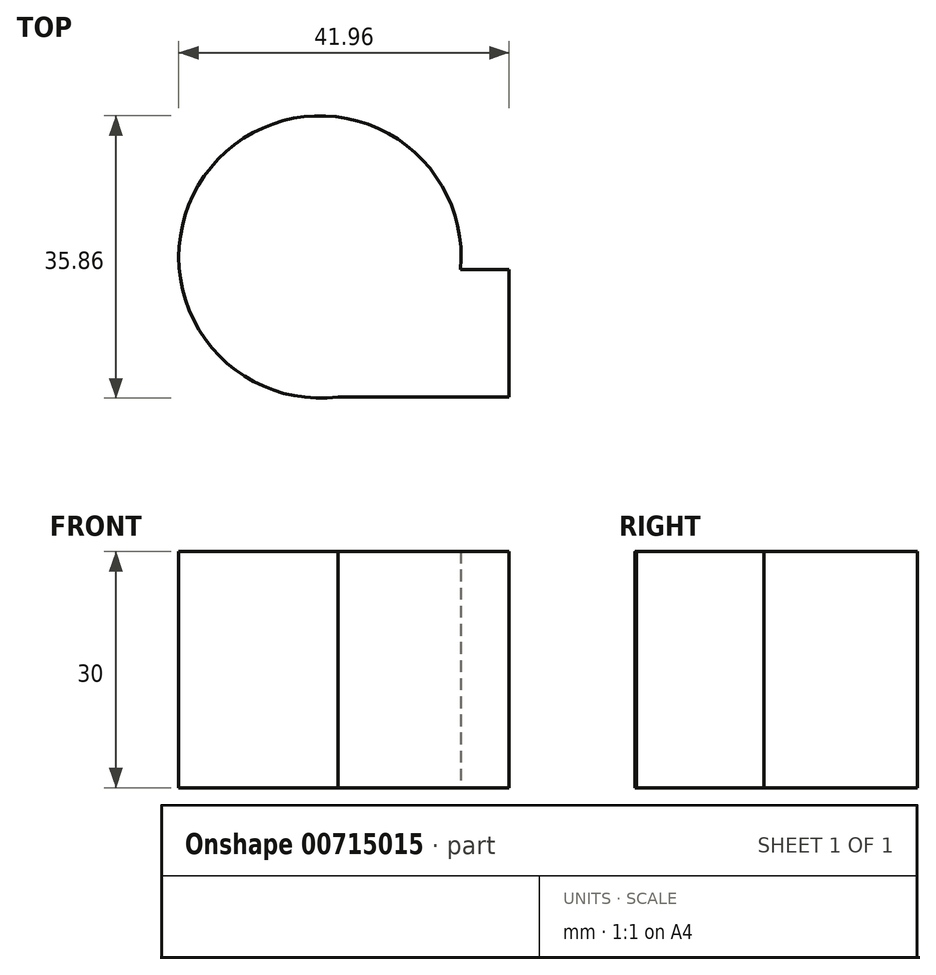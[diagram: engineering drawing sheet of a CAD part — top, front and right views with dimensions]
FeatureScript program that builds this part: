
annotation { "Feature Type Name" : "Feature", "Feature Type Description" : "" }
export const myFeature = defineFeature(function(context is Context, id is Id, definition is map)
    precondition{}
    {
        {
            var Q0;
            Q0=qCreatedBy(makeId("Top.planeOp"),FACE);
            var sketch = newSketch(context, id + "F0", { "sketchPlane" : qUnion([Q0])});
            skLineSegment(sketch, "E0.bottom", {"start": v(-31.12, 24.11) * mm, "end": v(50.55, 24.11) * mm});
            skLineSegment(sketch, "E0.top", {"start": v(-31.12, -36.94) * mm, "end": v(50.55, -36.94) * mm});
            skLineSegment(sketch, "E0.left", {"start": v(-31.12, 24.11) * mm, "end": v(-31.12, -36.94) * mm});
            skLineSegment(sketch, "E0.right", {"start": v(50.55, 24.11) * mm, "end": v(50.55, -36.94) * mm});
            skLineSegment(sketch, "E1.bottom", {"start": v(0, -1.6) * mm, "end": v(24.03, -1.6) * mm});
            skLineSegment(sketch, "E1.top", {"start": v(0, -17.78) * mm, "end": v(24.03, -17.78) * mm});
            skLineSegment(sketch, "E1.left", {"start": v(0, -1.6) * mm, "end": v(0, -17.78) * mm});
            skLineSegment(sketch, "E1.right", {"start": v(24.03, -1.6) * mm, "end": v(24.03, -17.78) * mm});
            skCircle(sketch, "E2", {"center": v(0, 0) * mm, "radius": 17.93 * mm});
            skSolve(sketch);
        }
        {
            var Q0;
            {var subQ0=sQuery(id+"F0.wireOp",EDGE,"E1.left");Q0=makeQuery(id+"F0.imprint","IMPRINT",FACE,{"disambiguationData":[TD([[makeQuery(id+"F0.imprint","IMPRINT",EDGE,{"derivedFrom":subQ0}),1.0]])]});}
            var Q1;
            {var subQ0=sQuery(id+"F0.wireOp",EDGE,"E1.right");Q1=makeQuery(id+"F0.imprint","IMPRINT",FACE,{"disambiguationData":[TD([[makeQuery(id+"F0.imprint","IMPRINT",EDGE,{"derivedFrom":subQ0}),-1.0]])]});}
            var Q2;
            {var subQ0=sQuery(id+"F0.wireOp",EDGE,"E1.left");Q2=makeQuery(id+"F0.imprint","IMPRINT",FACE,{"disambiguationData":[TD([[makeQuery(id+"F0.imprint","IMPRINT",EDGE,{"derivedFrom":subQ0}),-1.0]])]});}
            extrude(context, id + "F1", {"entities" : qUnion([Q0, Q1, Q2]), "depth" : 30 * mm, "offsetDistance" : 25.4 * mm});
        }
    });
